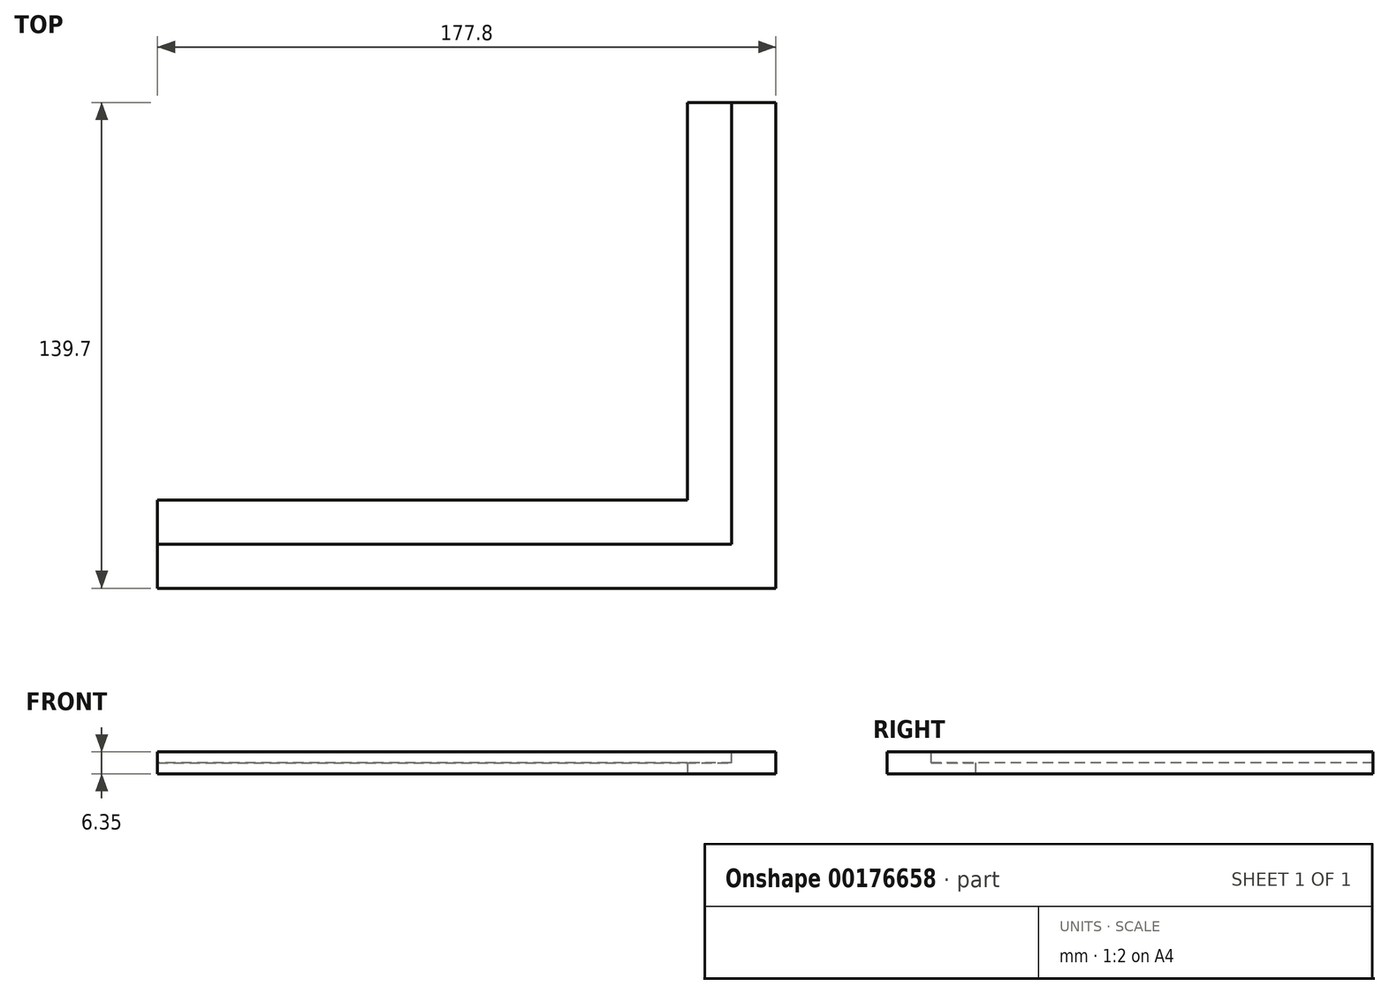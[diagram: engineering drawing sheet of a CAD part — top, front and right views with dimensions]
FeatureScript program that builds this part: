
annotation { "Feature Type Name" : "Feature", "Feature Type Description" : "" }
export const myFeature = defineFeature(function(context is Context, id is Id, definition is map)
    precondition{}
    {
        {
            var Q0;
            Q0=qCreatedBy(makeId("Top.planeOp"),FACE);
            var sketch = newSketch(context, id + "F0", { "sketchPlane" : qUnion([Q0])});
            skLineSegment(sketch, "E0.bottom", {"start": v(0, 0) * mm, "end": v(-177.8, 0) * mm});
            skLineSegment(sketch, "E0.top", {"start": v(0, 139.7) * mm, "end": v(-25.4, 139.7) * mm});
            skLineSegment(sketch, "E0.left", {"start": v(0, 0) * mm, "end": v(0, 139.7) * mm});
            skLineSegment(sketch, "E0.right", {"start": v(-177.8, 0) * mm, "end": v(-177.8, 25.4) * mm});
            skLineSegment(sketch, "E1.top", {"start": v(-25.4, 25.4) * mm, "end": v(-177.8, 25.4) * mm});
            skLineSegment(sketch, "E1.left", {"start": v(-25.4, 139.7) * mm, "end": v(-25.4, 25.4) * mm});
            skSolve(sketch);
        }
        {
            var Q0;
            Q0 = qSketchRegion(id + "F0", true);
            extrude(context, id + "F1", {"entities" : qUnion([Q0]), "depth" : 6.35 * mm});
        }
        {
            var Q0;
            Q0=makeQuery(id+"F1.opExtrude","CAP_FACE",FACE,{"disambiguationData":[OSD([sQuery(id+"F0.wireOp",EDGE,"E0.bottom"),sQuery(id+"F0.wireOp",EDGE,"E0.top"),sQuery(id+"F0.wireOp",EDGE,"E0.left"),sQuery(id+"F0.wireOp",EDGE,"E0.right"),sQuery(id+"F0.wireOp",EDGE,"E1.top"),sQuery(id+"F0.wireOp",EDGE,"E1.left")])],"isStart":false});
            var sketch = newSketch(context, id + "F2", { "sketchPlane" : qUnion([Q0])});
            skLineSegment(sketch, "E2.bottom", {"start": v(-177.8, 12.7) * mm, "end": v(-25.4, 12.7) * mm});
            skLineSegment(sketch, "E2.top", {"start": v(-177.8, 25.4) * mm, "end": v(-25.4, 25.4) * mm});
            skLineSegment(sketch, "E2.left", {"start": v(-177.8, 12.7) * mm, "end": v(-177.8, 25.4) * mm});
            skLineSegment(sketch, "E3.bottom", {"start": v(-12.7, 139.7) * mm, "end": v(-25.4, 139.7) * mm});
            skLineSegment(sketch, "E3.left", {"start": v(-12.7, 139.7) * mm, "end": v(-12.7, 25.4) * mm});
            skLineSegment(sketch, "E3.right", {"start": v(-25.4, 139.7) * mm, "end": v(-25.4, 25.4) * mm});
            skLineSegment(sketch, "E4.top", {"start": v(-12.7, 12.7) * mm, "end": v(-25.4, 12.7) * mm});
            skLineSegment(sketch, "E4.left", {"start": v(-12.7, 25.4) * mm, "end": v(-12.7, 12.7) * mm});
            skSolve(sketch);
        }
        {
            var Q0;
            Q0 = qSketchRegion(id + "F2", true);
            extrude(context, id + "F3", {"entities" : qUnion([Q0]), "operationType" : NewBodyOperationType.REMOVE, "oppositeDirection" : true, "depth" : 3.17 * mm});
        }
    });
